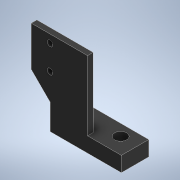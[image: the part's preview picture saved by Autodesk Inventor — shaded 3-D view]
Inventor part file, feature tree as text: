
AUTODESK INVENTOR PART (.ipt)
format: ipt  version: 2021 (Build 250183000, 183)  size: 141,312 bytes
history: native  units: mm
features: extrude x3, sketch x3, chamfer x1
ambient origin geometry x8: Origin, YZ Plane, XZ Plane, XY Plane, X Axis, Y Axis, Z Axis, Center Point
bodies: Solid1 (feature_tree)
feature tree (7):
  extrude  "Extrusion1"  Depth=22.5mm
  extrude  "Extrusion2"  Depth=1.5mm
  extrude  "Extrusion3"  Depth=5.0mm
  chamfer  "Chamfer1"  Distance=5.0mm
  sketch  "Sketch1"  dims[d1=4.0mm d2=22.5mm]
  sketch  "Sketch2"  dims[d3=1.5mm d4=13.825mm]
  sketch  "Sketch3"  dims[d5=6.5mm d6=2.0mm d7=5.0mm d8=24.0mm d9=15.0mm d10=5.0mm d11=1.5mm d12=0.0mm d13=5.8mm d14=0.0mm d15=14.5mm d16=3.0mm d17=3.2mm d18=0.0mm d19=0.0mm d20=5.0mm d21=2.0mm d22=45.0deg]
